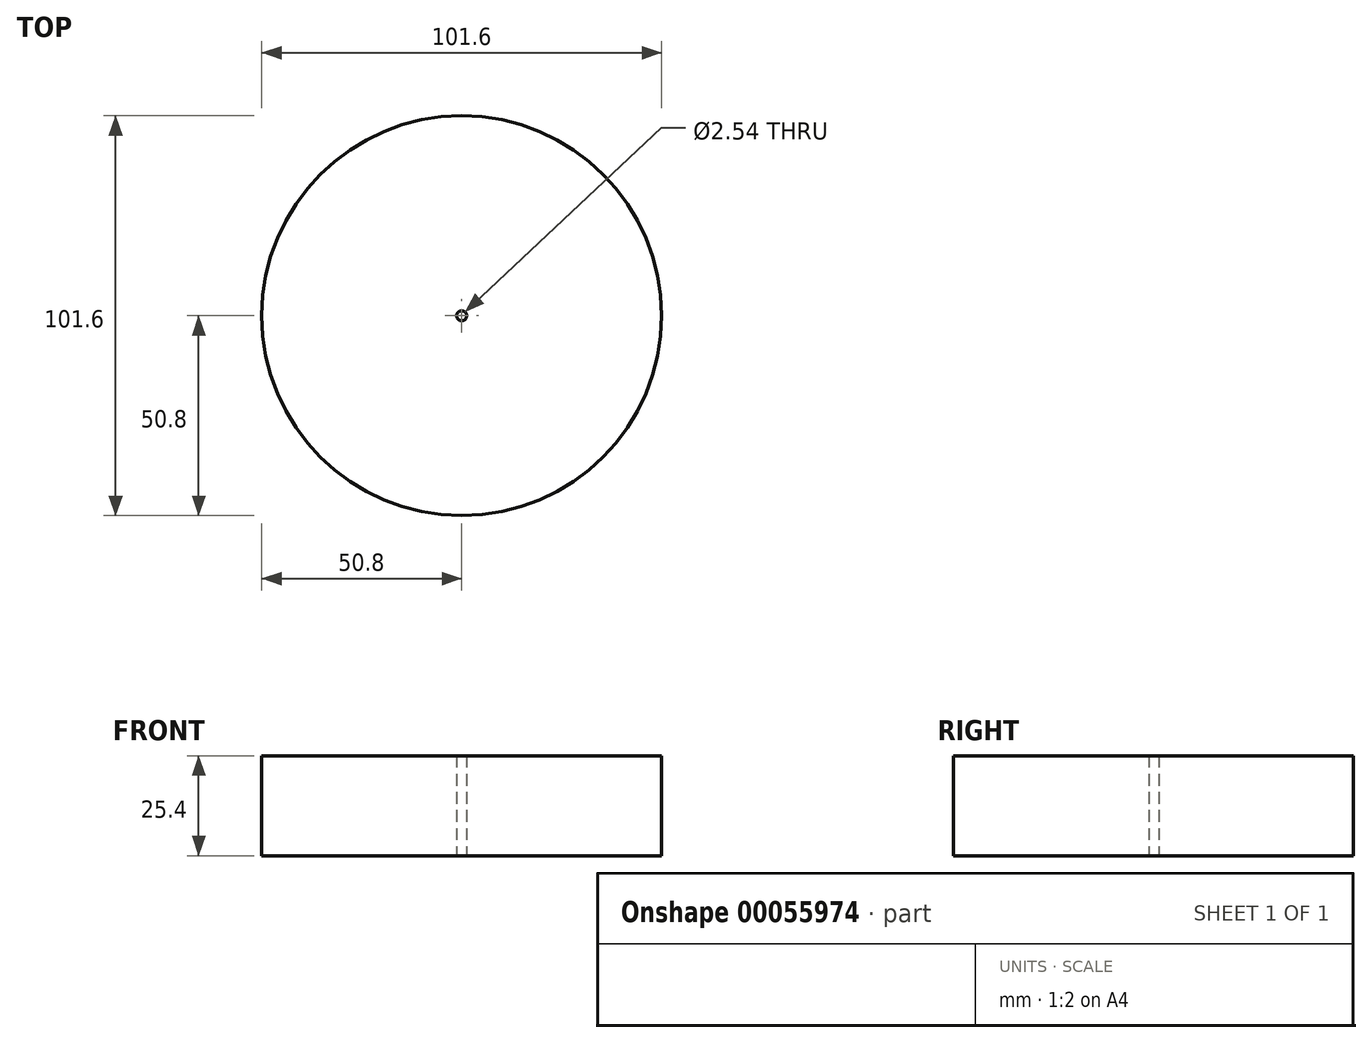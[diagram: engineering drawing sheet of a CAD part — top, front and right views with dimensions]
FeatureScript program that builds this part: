
annotation { "Feature Type Name" : "Feature", "Feature Type Description" : "" }
export const myFeature = defineFeature(function(context is Context, id is Id, definition is map)
    precondition{}
    {
        {
            var Q0;
            Q0=qCreatedBy(makeId("Top.planeOp"),FACE);
            var sketch = newSketch(context, id + "F0", { "sketchPlane" : qUnion([Q0])});
            skCircle(sketch, "E0", {"center": v(0, 0) * mm, "radius": 50.8 * mm});
            skCircle(sketch, "E1", {"center": v(0, 0) * mm, "radius": 1.27 * mm});
            skSolve(sketch);
        }
        {
            var Q0;
            Q0 = qSketchRegion(id + "F0", true);
            extrude(context, id + "F1", {"entities" : qUnion([Q0]), "depth" : 25.4 * mm});
        }
    });
